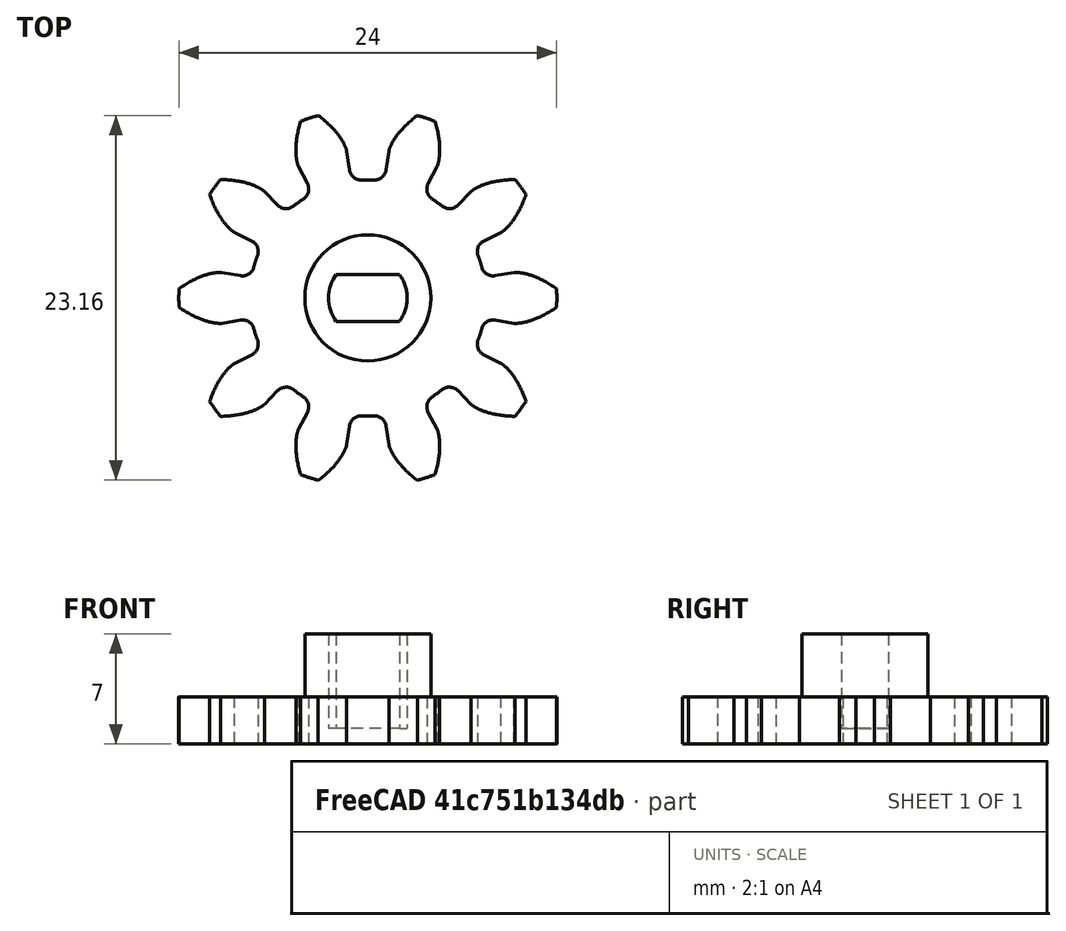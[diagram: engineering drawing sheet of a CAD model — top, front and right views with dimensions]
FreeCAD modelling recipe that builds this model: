
FCSTD DOCUMENT  (FreeCAD 0.16R5484 (Git))
Label: Motor_horn (otra copia)
License: CreativeCommons Attribution-ShareAlike
LicenseURL: http://creativecommons.org/licenses/by-sa/4.0/
objects: Part::Feature×2, Part::Part2DObjectPython×1, Part::Extrusion×1, Part::Cylinder×1, Part::Fuse×1, Part::Cut×1
note: 7 computed .brp shape members not serialized (recipe doc carries the construction recipe); baked Part::Feature solids carry a one-line shape summary decoded from their .brp

FEATURE [Part::Part2DObjectPython] InvoluteGear  # Draft 2D object (typed FeaturePython)
  ExternalGear = true
  HighPrecision = true
  Modules = 2
  NumberOfTeeth = 10
  PressureAngle = 20
FEATURE [Part::Feature] Cut001003002  label="Axis004"
  Placement = pos=(0,0,11) rot=(1,0,0;3.14159rad)
  shape: bbox 5 x 5 x 10 mm, 7 faces (baked)
FEATURE [Part::Extrusion] Extrude
  Base = -> InvoluteGear
  Dir = (0,0,3)
  Solid = true
FEATURE [Part::Cylinder] Cylinder002  label="Cilindro002"
  Angle = 360
  Height = 7
  Radius = 4
FEATURE [Part::Fuse] Fusion002
  Base = -> Extrude
  Tool = -> Cylinder002
FEATURE [Part::Feature] Cut001003003001  label="28BYJ-48_gear_horn"
  shape: bbox 24.01 x 23.17 x 7 mm, 109 faces (baked)
FEATURE [Part::Cut] Cut001003003  label="Engranaje"
  Base = -> Fusion002
  Tool = -> Cut001003002
